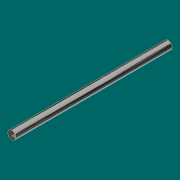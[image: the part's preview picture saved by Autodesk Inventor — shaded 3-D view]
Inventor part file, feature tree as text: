
AUTODESK INVENTOR PART (.ipt)
format: ipt  version: 2017 (Build 210142000, 142)  size: 71,168 bytes
history: native  units: in
note: dims shown in document units (in); Inventor stores cm internally (conversion verified against a paired STEP export)
features: extrude x1, sketch x1
ambient origin geometry x8: Origin, YZ Plane, XZ Plane, XY Plane, X Axis, Y Axis, Z Axis, Center Point
bodies: Solid1 (feature_tree)
feature tree (2):
  extrude  "Extrusion1"  Depth=24.0in TaperAngle=0.0deg
  sketch  "Sketch1"  dims[d0=1.25in d1=24.0in d2=0.0in]
